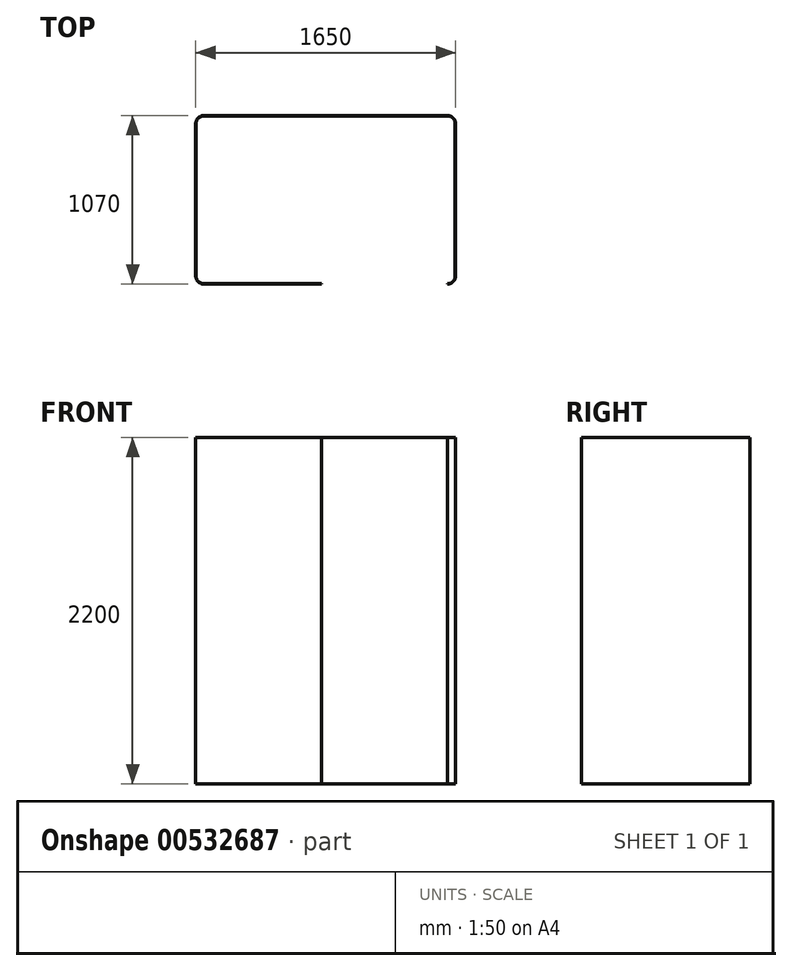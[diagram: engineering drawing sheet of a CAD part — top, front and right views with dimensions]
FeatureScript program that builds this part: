
annotation { "Feature Type Name" : "Feature", "Feature Type Description" : "" }
export const myFeature = defineFeature(function(context is Context, id is Id, definition is map)
    precondition{}
    {
        {
            var Q0;
            Q0=qCreatedBy(makeId("Top.planeOp"),FACE);
            var sketch = newSketch(context, id + "F0", { "sketchPlane" : qUnion([Q0])});
            skLineSegment(sketch, "E0.bottom", {"start": v(775, 535) * mm, "end": v(-775, 535) * mm});
            skLineSegment(sketch, "E0.top", {"start": v(-27, -535) * mm, "end": v(-775, -535) * mm});
            skLineSegment(sketch, "E0.left", {"start": v(825, 485) * mm, "end": v(825, -485) * mm});
            skLineSegment(sketch, "E0.right", {"start": v(-825, 485) * mm, "end": v(-825, -485) * mm});
            skPoint(sketch, "E0.middle", {"position": v(0, 0) * mm});
            skLineSegment(sketch, "E1.0", {"start": v(773, 533) * mm, "end": v(-773, 533) * mm});
            skLineSegment(sketch, "E1.1", {"start": v(823, 483) * mm, "end": v(823, -483) * mm});
            skLineSegment(sketch, "E1.2", {"start": v(-27, -533) * mm, "end": v(-773, -533) * mm});
            skLineSegment(sketch, "E1.3", {"start": v(-823, 483) * mm, "end": v(-823, -483) * mm});
            skPoint(sketch, "E2.visualSharp", {"position": v(-823, 533) * mm});
            skArc(sketch, "E2.filletArc", {"start": v(-773, 533) * mm, "mid": v(-808.36, 518.36) * mm, "end": v(-823, 483) * mm});
            skPoint(sketch, "E3.visualSharp", {"position": v(-825, 535) * mm});
            skArc(sketch, "E3.filletArc", {"start": v(-775, 535) * mm, "mid": v(-810.36, 520.36) * mm, "end": v(-825, 485) * mm});
            skPoint(sketch, "E4.visualSharp", {"position": v(823, 533) * mm});
            skArc(sketch, "E4.filletArc", {"start": v(823, 483) * mm, "mid": v(808.36, 518.36) * mm, "end": v(773, 533) * mm});
            skPoint(sketch, "E5.visualSharp", {"position": v(825, 535) * mm});
            skArc(sketch, "E5.filletArc", {"start": v(825, 485) * mm, "mid": v(810.36, 520.36) * mm, "end": v(775, 535) * mm});
            skPoint(sketch, "E6.visualSharp", {"position": v(825, -535) * mm});
            skArc(sketch, "E6.filletArc", {"start": v(775, -535) * mm, "mid": v(810.36, -520.36) * mm, "end": v(825, -485) * mm});
            skPoint(sketch, "E7.visualSharp", {"position": v(823, -533) * mm});
            skArc(sketch, "E7.filletArc", {"start": v(773, -533) * mm, "mid": v(808.36, -518.36) * mm, "end": v(823, -483) * mm});
            skPoint(sketch, "E8.visualSharp", {"position": v(-825, -535) * mm});
            skArc(sketch, "E8.filletArc", {"start": v(-825, -485) * mm, "mid": v(-810.36, -520.36) * mm, "end": v(-775, -535) * mm});
            skPoint(sketch, "E9.visualSharp", {"position": v(-823, -533) * mm});
            skArc(sketch, "E9.filletArc", {"start": v(-823, -483) * mm, "mid": v(-808.36, -518.36) * mm, "end": v(-773, -533) * mm});
            skPoint(sketch, "E10", {"position": v(-27, -535) * mm});
            skPoint(sketch, "E11", {"position": v(-27, -533) * mm});
            skLineSegment(sketch, "E12", {"start": v(-27, -533) * mm, "end": v(-27, -535) * mm});
            skLineSegment(sketch, "E13", {"start": v(775, -535) * mm, "end": v(772.99, -535) * mm});
            skLineSegment(sketch, "E14", {"start": v(772.99, -535) * mm, "end": v(773, -533) * mm});
            skSolve(sketch);
        }
        {
            var Q0;
            Q0 = qSketchRegion(id + "F0", true);
            extrude(context, id + "F1", {"entities" : qUnion([Q0]), "depth" : 2200 * mm, "offsetDistance" : 25 * mm});
        }
    });
